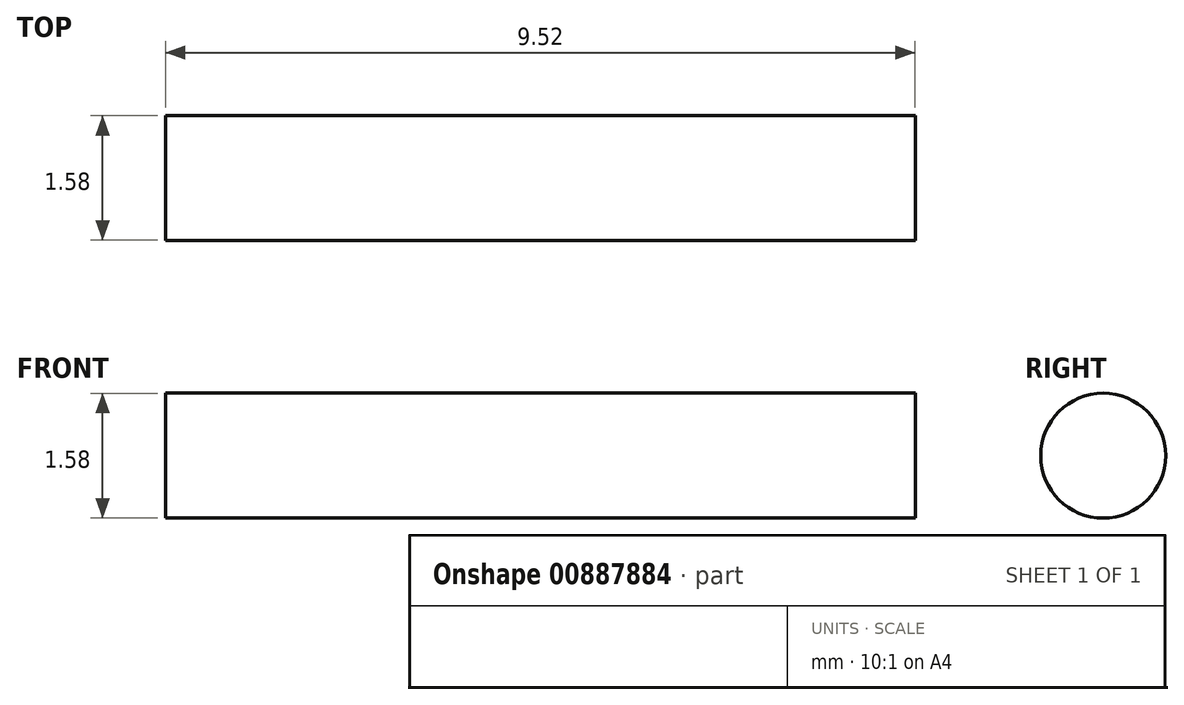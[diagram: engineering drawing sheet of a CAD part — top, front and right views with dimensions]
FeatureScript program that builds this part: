
annotation { "Feature Type Name" : "Feature", "Feature Type Description" : "" }
export const myFeature = defineFeature(function(context is Context, id is Id, definition is map)
    precondition{}
    {
        {
            var Q0;
            Q0=qCreatedBy(makeId("Right.planeOp"),FACE);
            var sketch = newSketch(context, id + "F0", { "sketchPlane" : qUnion([Q0])});
            skCircle(sketch, "E0", {"center": v(0, 0) * mm, "radius": 0.8 * mm});
            skSolve(sketch);
        }
        {
            var Q0;
            Q0=makeQuery(id+"F0.imprint","IMPRINT",FACE,{"disambiguationData":[TD([[makeQuery(id+"F0.imprint","IMPRINT",EDGE,{"derivedFrom":sQuery(id+"F0.wireOp",EDGE,"E0")}),1.0]])]});
            extrude(context, id + "F1", {"entities" : qUnion([Q0]), "depth" : 9.52 * mm, "offsetDistance" : 25.4 * mm, "symmetric" : true});
        }
    });
